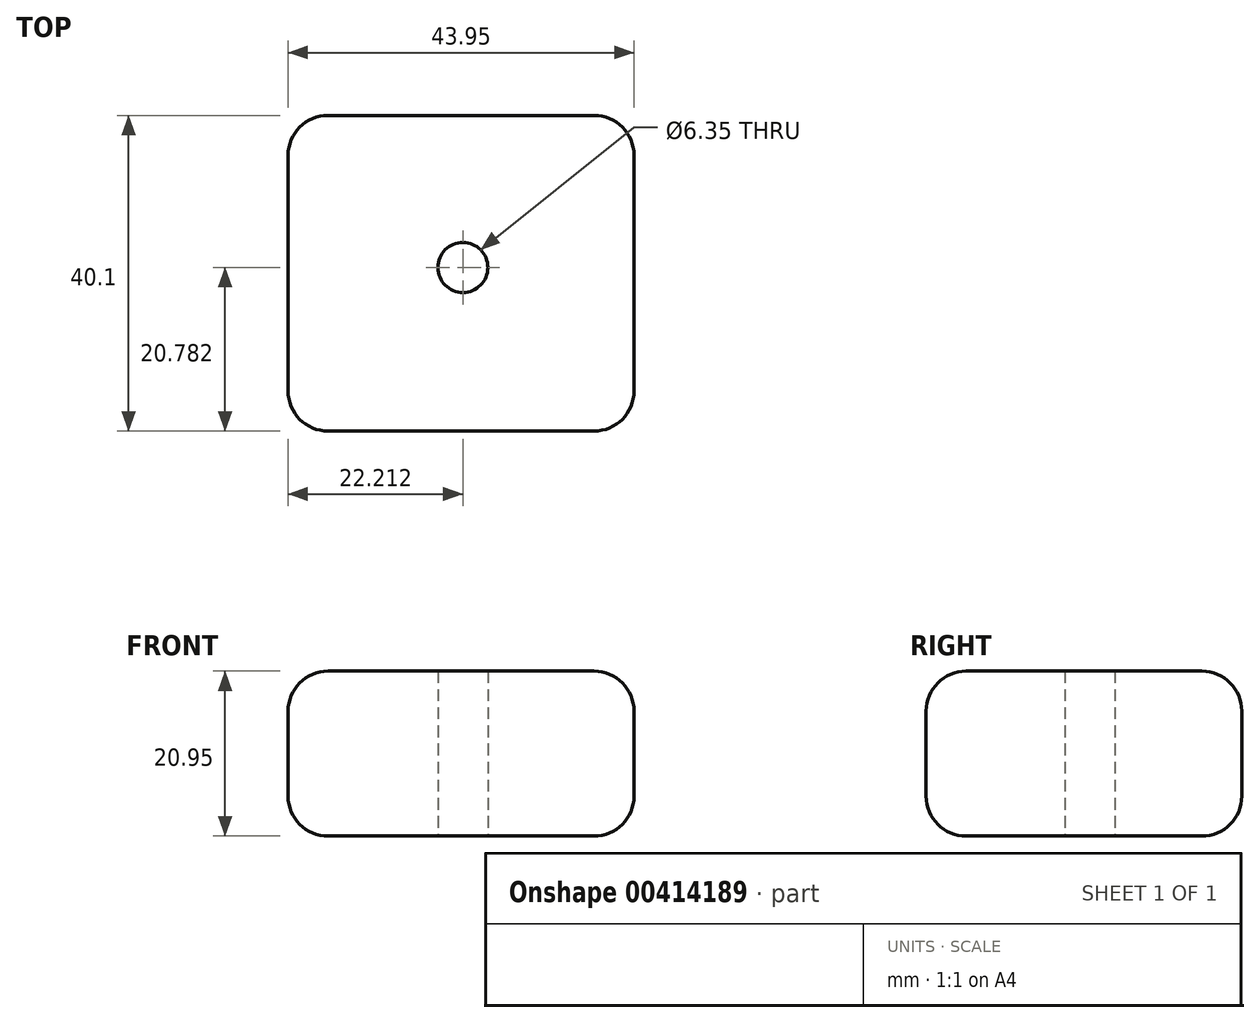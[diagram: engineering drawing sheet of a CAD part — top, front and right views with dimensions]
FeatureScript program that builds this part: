
annotation { "Feature Type Name" : "Feature", "Feature Type Description" : "" }
export const myFeature = defineFeature(function(context is Context, id is Id, definition is map)
    precondition{}
    {
        {
            var Q0;
            Q0=qCreatedBy(makeId("Top.planeOp"),FACE);
            var sketch = newSketch(context, id + "F0", { "sketchPlane" : qUnion([Q0])});
            skLineSegment(sketch, "E0.bottom", {"start": v(-27.72, 24.25) * mm, "end": v(16.23, 24.25) * mm});
            skLineSegment(sketch, "E0.top", {"start": v(-27.72, -15.85) * mm, "end": v(16.23, -15.85) * mm});
            skLineSegment(sketch, "E0.left", {"start": v(-27.72, 24.25) * mm, "end": v(-27.72, -15.85) * mm});
            skLineSegment(sketch, "E0.right", {"start": v(16.23, 24.25) * mm, "end": v(16.23, -15.85) * mm});
            skSolve(sketch);
        }
        {
            var Q0;
            Q0=qCreatedBy(makeId("Front.planeOp"),FACE);
            var sketch = newSketch(context, id + "F1", { "sketchPlane" : qUnion([Q0])});
            skLineSegment(sketch, "E1", {"start": v(0, 0) * mm, "end": v(0, 20.95) * mm});
            skSolve(sketch);
        }
        {
            var Q0;
            Q0=makeQuery(id+"F0.imprint","IMPRINT",FACE,{"disambiguationData":[TD([[makeQuery(id+"F0.imprint","IMPRINT",EDGE,{"derivedFrom":sQuery(id+"F0.wireOp",EDGE,"E0.bottom")}),-1.0]])]});
            var Q1;
            Q1=sQuery(id+"F1.wireOp",EDGE,"E1");
            sweep(context, id + "F2", {"profiles" : qUnion([Q0]), "path" : qUnion([Q1])});
        }
        {
            var Q0;
            Q0=makeQuery(id+"F2.opSweep","CAP_EDGE",EDGE,{"disambiguationData":[OSD([sQuery(id+"F0.wireOp",EDGE,"E0.left"),sQuery(id+"F1.wireOp",VERTEX,"E1.end")])],"isStart":false});
            var Q1;
            Q1=makeQuery(id+"F2.opSweep","CAP_EDGE",EDGE,{"disambiguationData":[OSD([sQuery(id+"F0.wireOp",EDGE,"E0.right"),sQuery(id+"F1.wireOp",VERTEX,"E1.end")])],"isStart":false});
            var Q2;
            Q2=makeQuery(id+"F2.opSweep","CAP_EDGE",EDGE,{"disambiguationData":[OSD([sQuery(id+"F0.wireOp",EDGE,"E0.bottom"),sQuery(id+"F1.wireOp",VERTEX,"E1.end")])],"isStart":false});
            var Q3;
            Q3=makeQuery(id+"F2.opSweep","CAP_EDGE",EDGE,{"disambiguationData":[OSD([sQuery(id+"F0.wireOp",EDGE,"E0.top"),sQuery(id+"F1.wireOp",VERTEX,"E1.end")])],"isStart":false});
            var Q4;
            Q4=makeQuery(id+"F2.opSweep","SWEPT_EDGE",EDGE,{"disambiguationData":[OSD([sQuery(id+"F0.wireOp",EDGE,"E0.top"),sQuery(id+"F0.wireOp",EDGE,"E0.right"),sQuery(id+"F1.wireOp",EDGE,"E1")])]});
            var Q5;
            Q5=makeQuery(id+"F2.opSweep","SWEPT_EDGE",EDGE,{"disambiguationData":[OSD([sQuery(id+"F0.wireOp",EDGE,"E0.top"),sQuery(id+"F0.wireOp",EDGE,"E0.left"),sQuery(id+"F1.wireOp",EDGE,"E1")])]});
            var Q6;
            Q6=makeQuery(id+"F2.opSweep","SWEPT_EDGE",EDGE,{"disambiguationData":[OSD([sQuery(id+"F0.wireOp",EDGE,"E0.bottom"),sQuery(id+"F0.wireOp",EDGE,"E0.left"),sQuery(id+"F1.wireOp",EDGE,"E1")])]});
            var Q7;
            Q7=makeQuery(id+"F2.opSweep","SWEPT_EDGE",EDGE,{"disambiguationData":[OSD([sQuery(id+"F0.wireOp",EDGE,"E0.bottom"),sQuery(id+"F0.wireOp",EDGE,"E0.right"),sQuery(id+"F1.wireOp",EDGE,"E1")])]});
            var Q8;
            Q8=makeQuery(id+"F2.opSweep","CAP_EDGE",EDGE,{"disambiguationData":[OSD([sQuery(id+"F0.wireOp",EDGE,"E0.bottom"),sQuery(id+"F1.wireOp",VERTEX,"E1.start")])],"isStart":true});
            var Q9;
            Q9=makeQuery(id+"F2.opSweep","CAP_EDGE",EDGE,{"disambiguationData":[OSD([sQuery(id+"F0.wireOp",EDGE,"E0.left"),sQuery(id+"F1.wireOp",VERTEX,"E1.start")])],"isStart":true});
            var Q10;
            Q10=makeQuery(id+"F2.opSweep","CAP_EDGE",EDGE,{"disambiguationData":[OSD([sQuery(id+"F0.wireOp",EDGE,"E0.top"),sQuery(id+"F1.wireOp",VERTEX,"E1.start")])],"isStart":true});
            var Q11;
            Q11=makeQuery(id+"F2.opSweep","CAP_EDGE",EDGE,{"disambiguationData":[OSD([sQuery(id+"F0.wireOp",EDGE,"E0.right"),sQuery(id+"F1.wireOp",VERTEX,"E1.start")])],"isStart":true});
            fillet(context, id + "F3", {"entities" : qUnion([Q0, Q1, Q2, Q3, Q4, Q5, Q6, Q7, Q8, Q9, Q10, Q11]), "radius" : 5.08 * mm, "tangentPropagation" : true, "allowEdgeOverflow" : false});
        }
        {
            var Q0;
            Q0=makeQuery(id+"F2.opSweep","CAP_FACE",FACE,{"disambiguationData":[OSD([sQuery(id+"F0.wireOp",EDGE,"E0.bottom"),sQuery(id+"F0.wireOp",EDGE,"E0.top"),sQuery(id+"F0.wireOp",EDGE,"E0.left"),sQuery(id+"F0.wireOp",EDGE,"E0.right"),sQuery(id+"F1.wireOp",VERTEX,"E1.end")])],"isStart":false});
            var sketch = newSketch(context, id + "F4", { "sketchPlane" : qUnion([Q0])});
            skCircle(sketch, "E2", {"center": v(-5.5, 4.93) * mm, "radius": 12.22 * mm});
            skSolve(sketch);
        }
        {
            var Q0;
            Q0=sQuery(id+"F4.wireOp",VERTEX,"E2.center");
            var Q1;
            Q1=makeQuery(id+"F2.opSweep","SWEPT_BODY",BODY,{"disambiguationData":[OSD([sQuery(id+"F0.wireOp",EDGE,"E0.bottom"),sQuery(id+"F0.wireOp",EDGE,"E0.top"),sQuery(id+"F0.wireOp",EDGE,"E0.left"),sQuery(id+"F0.wireOp",EDGE,"E0.right"),sQuery(id+"F1.wireOp",EDGE,"E1")])]});
            hole(context, id + "F5", {"style" : HoleStyle.SIMPLE, "endStyle" : HoleEndStyle.THROUGH, "holeDiameter" : 6.35 * mm, "isTappedThrough" : true, "tappedDepth" : 12.7 * mm, "tapClearance" : 3, "locations" : qUnion([Q0]), "scope" : qUnion([Q1]), "startStyle" : HoleStartStyle.PART});
        }
    });
